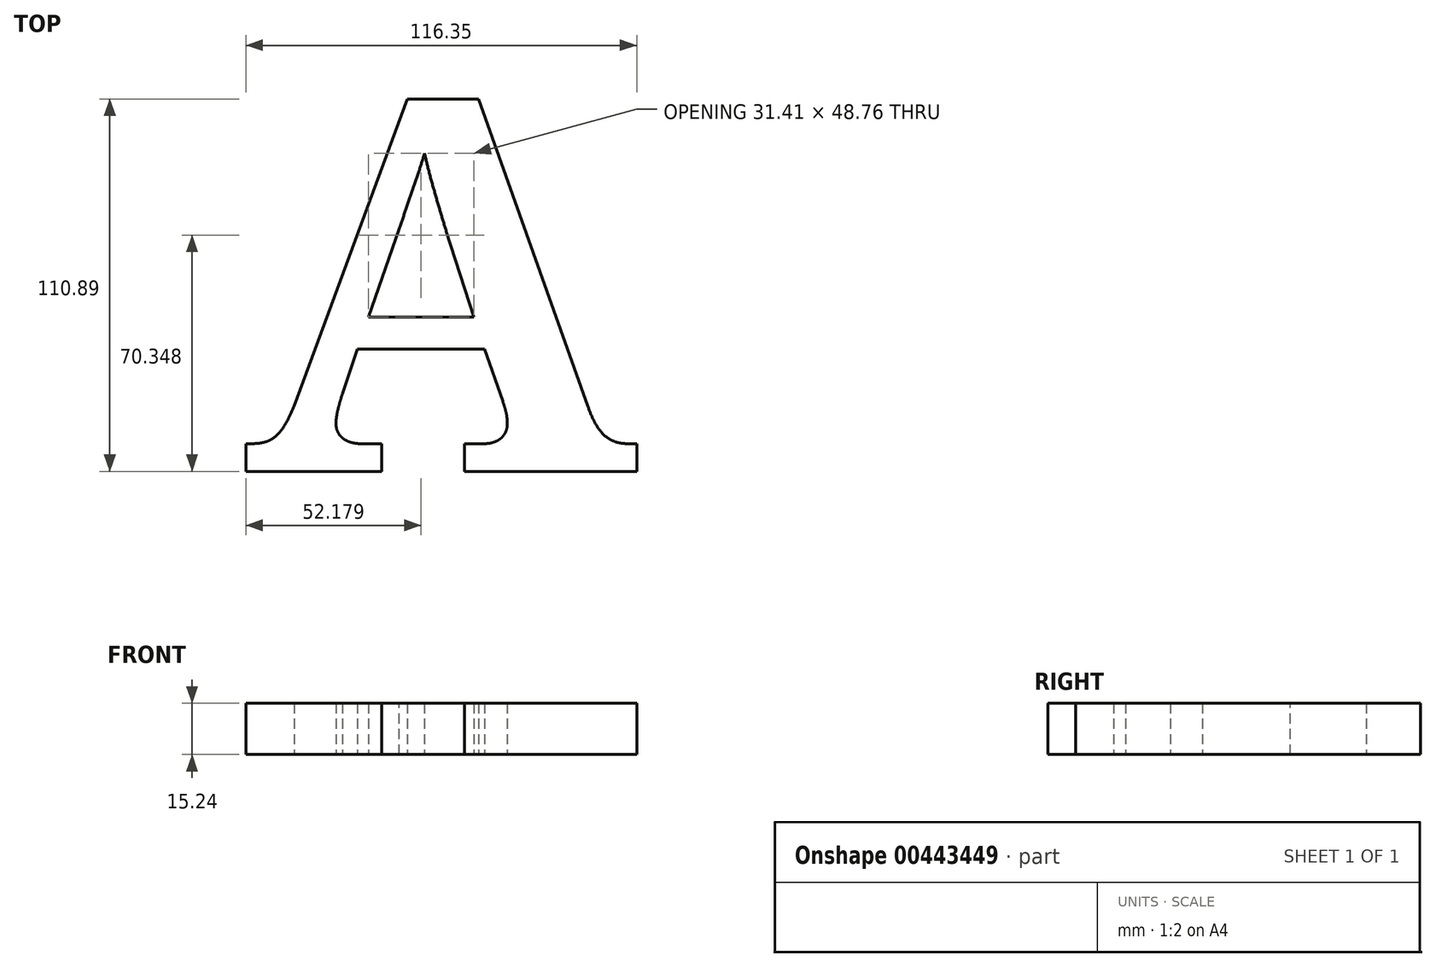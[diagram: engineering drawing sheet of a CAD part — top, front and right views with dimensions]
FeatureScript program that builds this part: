
annotation { "Feature Type Name" : "Feature", "Feature Type Description" : "" }
export const myFeature = defineFeature(function(context is Context, id is Id, definition is map)
    precondition{}
    {
        {
            var Q0;
            Q0=qCreatedBy(makeId("Top.planeOp"),FACE);
            var sketch = newSketch(context, id + "F0", { "sketchPlane" : qUnion([Q0])});
            skText(sketch, "E0", { "text": "A", "fontName": "NotoSerif-Bold.ttf"});
            const initialGuessF0  = {"E0": [-0.06265, -0.05592, 1, 0, 0.11184]};
            skSetInitialGuess(sketch, initialGuessF0);
            skSolve(sketch);
        }
        {
            var Q0;
            Q0=makeQuery(id+"F0.imprint","IMPRINT",FACE,{"disambiguationData":[TD([[makeQuery(id+"F0.imprint","IMPRINT",EDGE,{"derivedFrom":sQuery(id+"F0.wireOp",EDGE,"E0.sketch_text.stroke-0")}),-1.0]])]});
            extrude(context, id + "F1", {"entities" : qUnion([Q0]), "depth" : 15.24 * mm, "offsetDistance" : 25.4 * mm});
        }
    });
